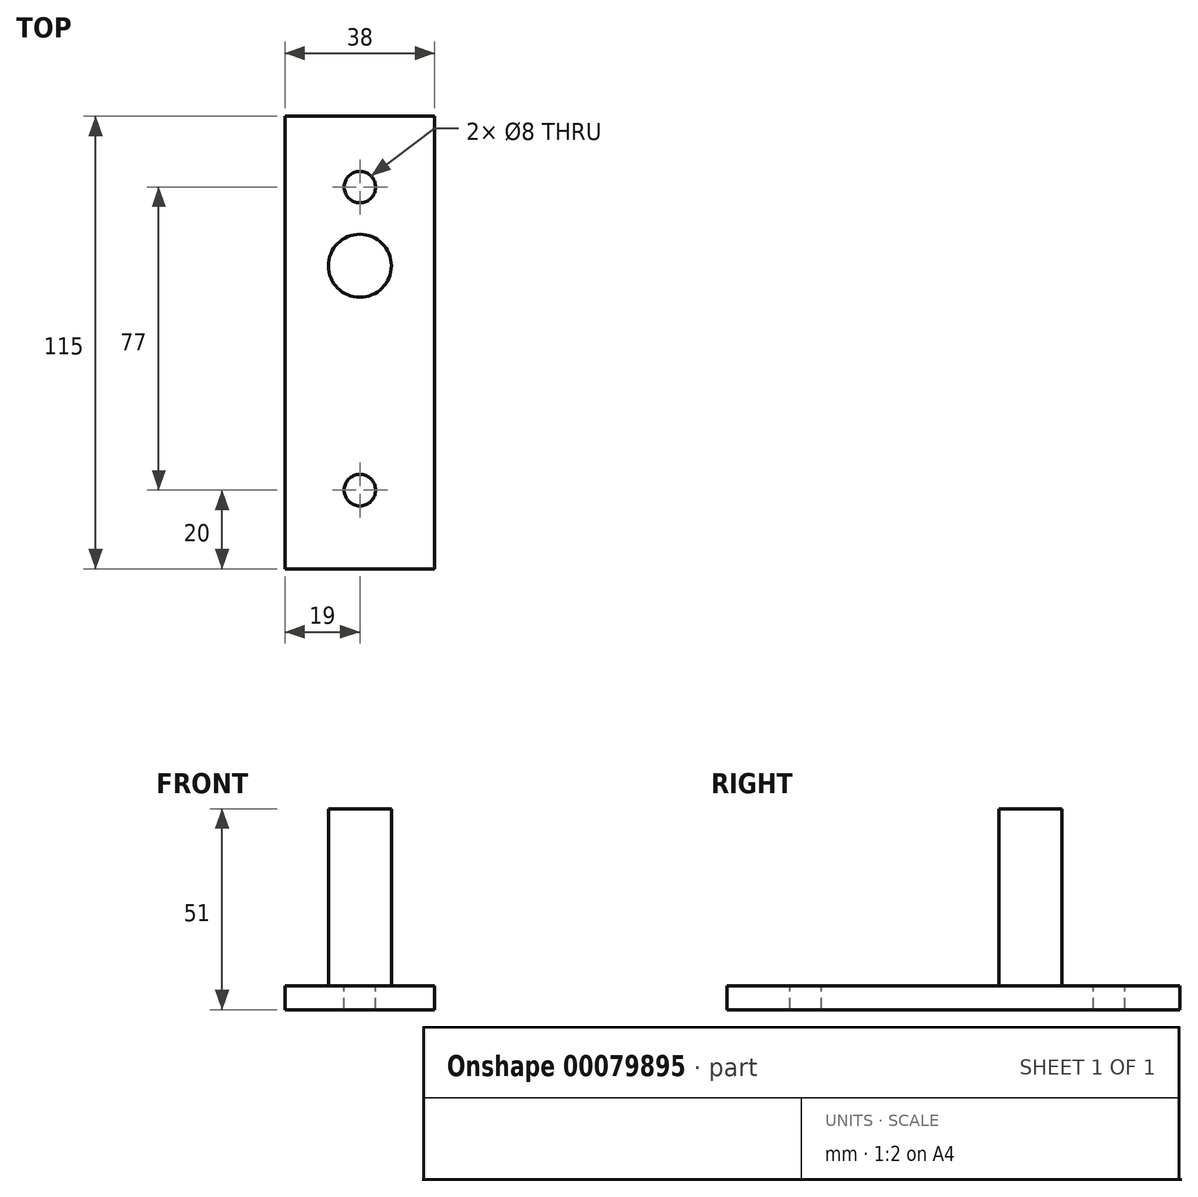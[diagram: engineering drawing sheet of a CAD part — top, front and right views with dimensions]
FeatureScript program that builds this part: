
annotation { "Feature Type Name" : "Feature", "Feature Type Description" : "" }
export const myFeature = defineFeature(function(context is Context, id is Id, definition is map)
    precondition{}
    {
        {
            var Q0;
            Q0=qCreatedBy(makeId("Top.planeOp"),FACE);
            var sketch = newSketch(context, id + "F0", { "sketchPlane" : qUnion([Q0])});
            skLineSegment(sketch, "E0", {"start": v(0, 57.5) * mm, "end": v(19, 57.5) * mm});
            skLineSegment(sketch, "E1", {"start": v(19, 57.5) * mm, "end": v(19, 0) * mm});
            skLineSegment(sketch, "E2.MirrorCS", {"start": v(0, 57.5) * mm, "end": v(-19, 57.5) * mm});
            skLineSegment(sketch, "E3.MirrorCS", {"start": v(-19, 57.5) * mm, "end": v(-19, 0) * mm});
            skLineSegment(sketch, "E4.MirrorCS", {"start": v(-19, -57.5) * mm, "end": v(-19, 0) * mm});
            skLineSegment(sketch, "E5.MirrorCS", {"start": v(0, -57.5) * mm, "end": v(-19, -57.5) * mm});
            skLineSegment(sketch, "E6.MirrorCS", {"start": v(0, -57.5) * mm, "end": v(19, -57.5) * mm});
            skLineSegment(sketch, "E7.MirrorCS", {"start": v(19, -57.5) * mm, "end": v(19, 0) * mm});
            skSolve(sketch);
        }
        {
            var Q0;
            Q0=makeQuery(id+"F0.imprint","IMPRINT",FACE,{"disambiguationData":[TD([[makeQuery(id+"F0.imprint","IMPRINT",EDGE,{"derivedFrom":sQuery(id+"F0.wireOp",EDGE,"E0")}),-1.0]])]});
            extrude(context, id + "F1", {"entities" : qUnion([Q0]), "depth" : 6 * mm});
        }
        {
            var Q0;
            Q0=makeQuery(id+"F1.opExtrude","CAP_FACE",FACE,{"disambiguationData":[OSD([sQuery(id+"F0.wireOp",EDGE,"E0"),sQuery(id+"F0.wireOp",EDGE,"E1"),sQuery(id+"F0.wireOp",EDGE,"E2.MirrorCS"),sQuery(id+"F0.wireOp",EDGE,"E3.MirrorCS"),sQuery(id+"F0.wireOp",EDGE,"E4.MirrorCS"),sQuery(id+"F0.wireOp",EDGE,"E5.MirrorCS"),sQuery(id+"F0.wireOp",EDGE,"E6.MirrorCS"),sQuery(id+"F0.wireOp",EDGE,"E7.MirrorCS")])],"isStart":false});
            var sketch = newSketch(context, id + "F2", { "sketchPlane" : qUnion([Q0])});
            skCircle(sketch, "E8", {"center": v(0, 19.5) * mm, "radius": 8 * mm});
            skCircle(sketch, "E9", {"center": v(0, 39.5) * mm, "radius": 4 * mm});
            skCircle(sketch, "E10", {"center": v(0, -37.5) * mm, "radius": 4 * mm});
            skSolve(sketch);
        }
        {
            var Q0;
            Q0=makeQuery(id+"F2.imprint","IMPRINT",FACE,{"disambiguationData":[TD([[makeQuery(id+"F2.imprint","IMPRINT",EDGE,{"derivedFrom":sQuery(id+"F2.wireOp",EDGE,"E8")}),1.0]])]});
            extrude(context, id + "F3", {"entities" : qUnion([Q0]), "operationType" : NewBodyOperationType.ADD, "depth" : 45 * mm});
        }
        {
            var Q0;
            Q0=makeQuery(id+"F2.imprint","IMPRINT",FACE,{"disambiguationData":[TD([[makeQuery(id+"F2.imprint","IMPRINT",EDGE,{"derivedFrom":sQuery(id+"F2.wireOp",EDGE,"E10")}),1.0]])]});
            var Q1;
            Q1=makeQuery(id+"F2.imprint","IMPRINT",FACE,{"disambiguationData":[TD([[makeQuery(id+"F2.imprint","IMPRINT",EDGE,{"derivedFrom":sQuery(id+"F2.wireOp",EDGE,"E9")}),1.0]])]});
            extrude(context, id + "F4", {"entities" : qUnion([Q0, Q1]), "operationType" : NewBodyOperationType.REMOVE, "oppositeDirection" : true, "depth" : 6 * mm});
        }
    });
